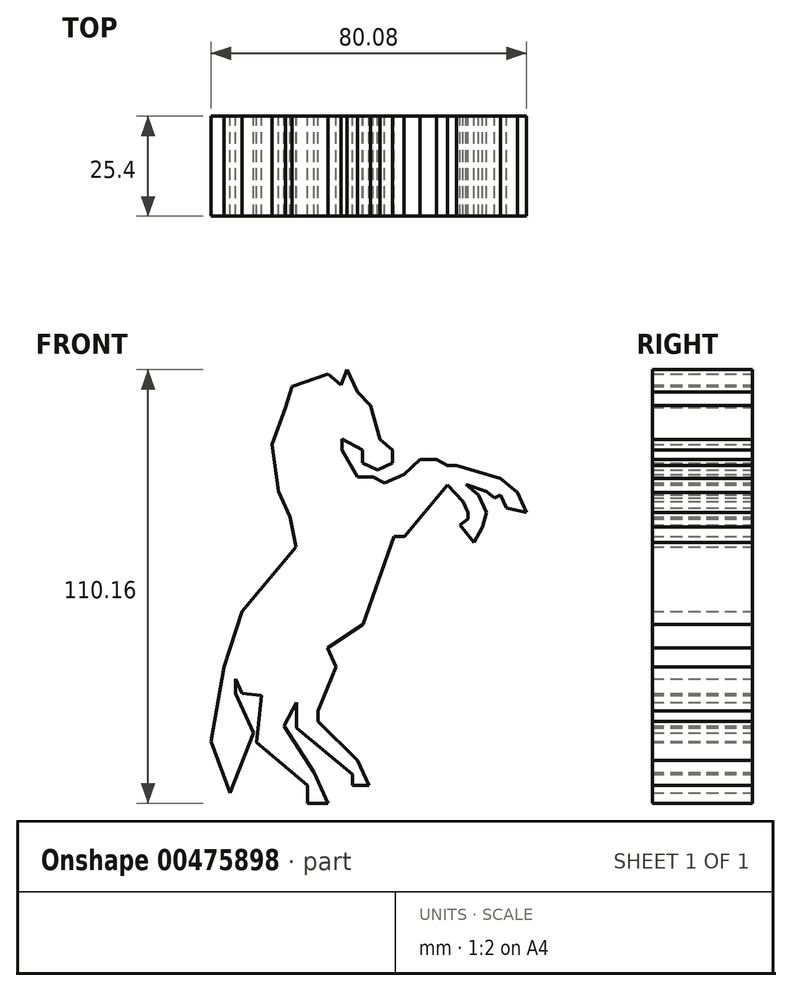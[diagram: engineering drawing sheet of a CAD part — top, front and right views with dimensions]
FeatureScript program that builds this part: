
annotation { "Feature Type Name" : "Feature", "Feature Type Description" : "" }
export const myFeature = defineFeature(function(context is Context, id is Id, definition is map)
    precondition{}
    {
        {
            var Q0;
            Q0=qCreatedBy(makeId("Front.planeOp"),FACE);
            var sketch = newSketch(context, id + "F0", { "sketchPlane" : qUnion([Q0])});
            skLineSegment(sketch, "E0", {"start": v(-2.68, 56.92) * mm, "end": v(0, 51.28) * mm});
            skLineSegment(sketch, "E1", {"start": v(0, 51.28) * mm, "end": v(3.22, 47.8) * mm});
            skLineSegment(sketch, "E2", {"start": v(3.22, 47.8) * mm, "end": v(5.64, 39.2) * mm});
            skLineSegment(sketch, "E3", {"start": v(5.64, 39.2) * mm, "end": v(8.86, 36.51) * mm});
            skLineSegment(sketch, "E4", {"start": v(8.86, 36.51) * mm, "end": v(8.86, 33.19) * mm});
            skLineSegment(sketch, "E5", {"start": v(8.86, 33.19) * mm, "end": v(5.1, 31.41) * mm});
            skLineSegment(sketch, "E6", {"start": v(5.1, 31.41) * mm, "end": v(1.26, 33.19) * mm});
            skLineSegment(sketch, "E7", {"start": v(1.26, 33.19) * mm, "end": v(1.26, 36.51) * mm});
            skLineSegment(sketch, "E8", {"start": v(1.26, 36.51) * mm, "end": v(-4, 39.32) * mm});
            skLineSegment(sketch, "E9", {"start": v(-4, 39.32) * mm, "end": v(-4, 36.51) * mm});
            skLineSegment(sketch, "E10", {"start": v(-4, 36.51) * mm, "end": v(0, 29.63) * mm});
            skLineSegment(sketch, "E11", {"start": v(0, 29.63) * mm, "end": v(3.95, 29.63) * mm});
            skLineSegment(sketch, "E12", {"start": v(3.95, 29.63) * mm, "end": v(6.8, 28.12) * mm});
            skLineSegment(sketch, "E13", {"start": v(6.8, 28.12) * mm, "end": v(11.8, 30.28) * mm});
            skLineSegment(sketch, "E14", {"start": v(11.8, 30.28) * mm, "end": v(15.79, 34.07) * mm});
            skLineSegment(sketch, "E15", {"start": v(15.79, 34.07) * mm, "end": v(20.03, 34.07) * mm});
            skLineSegment(sketch, "E16", {"start": v(20.03, 34.07) * mm, "end": v(22.83, 32.59) * mm});
            skLineSegment(sketch, "E17", {"start": v(22.83, 32.59) * mm, "end": v(25.15, 32.59) * mm});
            skLineSegment(sketch, "E18", {"start": v(25.15, 32.59) * mm, "end": v(36.34, 29.23) * mm});
            skLineSegment(sketch, "E19", {"start": v(36.34, 29.23) * mm, "end": v(40.54, 25.73) * mm});
            skLineSegment(sketch, "E20", {"start": v(40.54, 25.73) * mm, "end": v(42.86, 20.64) * mm});
            skLineSegment(sketch, "E21", {"start": v(42.86, 20.64) * mm, "end": v(37.86, 21.73) * mm});
            skLineSegment(sketch, "E22", {"start": v(37.86, 21.73) * mm, "end": v(36.34, 25.1) * mm});
            skLineSegment(sketch, "E23", {"start": v(36.34, 25.1) * mm, "end": v(34.74, 24.38) * mm});
            skLineSegment(sketch, "E24", {"start": v(34.74, 24.38) * mm, "end": v(32.76, 26.03) * mm});
            skLineSegment(sketch, "E25", {"start": v(32.76, 26.03) * mm, "end": v(27.5, 27.75) * mm});
            skLineSegment(sketch, "E26", {"start": v(27.5, 27.75) * mm, "end": v(30.68, 25.1) * mm});
            skLineSegment(sketch, "E27", {"start": v(30.68, 25.1) * mm, "end": v(32.7, 20.64) * mm});
            skLineSegment(sketch, "E28", {"start": v(32.7, 20.64) * mm, "end": v(31.7, 16.97) * mm});
            skLineSegment(sketch, "E29", {"start": v(31.7, 16.97) * mm, "end": v(29.58, 12.98) * mm});
            skLineSegment(sketch, "E30", {"start": v(29.58, 12.98) * mm, "end": v(26.03, 17.42) * mm});
            skLineSegment(sketch, "E31", {"start": v(26.03, 17.42) * mm, "end": v(28, 19) * mm});
            skLineSegment(sketch, "E32", {"start": v(28, 19) * mm, "end": v(28, 20.64) * mm});
            skLineSegment(sketch, "E33", {"start": v(28, 20.64) * mm, "end": v(26.76, 23.4) * mm});
            skLineSegment(sketch, "E34", {"start": v(26.76, 23.4) * mm, "end": v(22.83, 27.64) * mm});
            skLineSegment(sketch, "E35", {"start": v(22.83, 27.64) * mm, "end": v(11.92, 14.54) * mm});
            skLineSegment(sketch, "E36", {"start": v(11.92, 14.54) * mm, "end": v(9.23, 14.54) * mm});
            skLineSegment(sketch, "E37", {"start": v(9.23, 14.54) * mm, "end": v(1.4, -7.77) * mm});
            skLineSegment(sketch, "E38", {"start": v(1.4, -7.77) * mm, "end": v(-7.68, -13.79) * mm});
            skLineSegment(sketch, "E39", {"start": v(-7.68, -13.79) * mm, "end": v(-5.51, -18.58) * mm});
            skLineSegment(sketch, "E40", {"start": v(-5.51, -18.58) * mm, "end": v(-10.08, -29.81) * mm});
            skLineSegment(sketch, "E41", {"start": v(-10.08, -29.81) * mm, "end": v(-10.08, -32.43) * mm});
            skLineSegment(sketch, "E42", {"start": v(-10.08, -32.43) * mm, "end": v(0, -42.32) * mm});
            skLineSegment(sketch, "E43", {"start": v(0, -42.32) * mm, "end": v(2.87, -48.67) * mm});
            skLineSegment(sketch, "E44", {"start": v(2.87, -48.67) * mm, "end": v(-1.35, -48.67) * mm});
            skLineSegment(sketch, "E45", {"start": v(-1.35, -48.67) * mm, "end": v(-1.35, -45.96) * mm});
            skLineSegment(sketch, "E46", {"start": v(-1.35, -45.96) * mm, "end": v(-15.53, -34.14) * mm});
            skLineSegment(sketch, "E47", {"start": v(-15.53, -34.14) * mm, "end": v(-15.53, -27.63) * mm});
            skLineSegment(sketch, "E48", {"start": v(-15.53, -27.63) * mm, "end": v(-18.67, -33.54) * mm});
            skLineSegment(sketch, "E49", {"start": v(-18.67, -33.54) * mm, "end": v(-11.1, -45.37) * mm});
            skLineSegment(sketch, "E50", {"start": v(-11.1, -45.37) * mm, "end": v(-9.6, -48.67) * mm});
            skLineSegment(sketch, "E51", {"start": v(-9.6, -48.67) * mm, "end": v(-7.55, -53.24) * mm});
            skLineSegment(sketch, "E52", {"start": v(-7.55, -53.24) * mm, "end": v(-12.7, -53.24) * mm});
            skLineSegment(sketch, "E53", {"start": v(-12.7, -53.24) * mm, "end": v(-12.7, -48.67) * mm});
            skLineSegment(sketch, "E54", {"start": v(-12.7, -48.67) * mm, "end": v(-25.7, -37.83) * mm});
            skLineSegment(sketch, "E55", {"start": v(-25.7, -37.83) * mm, "end": v(-24.48, -25.89) * mm});
            skLineSegment(sketch, "E56", {"start": v(-24.48, -25.89) * mm, "end": v(-29.31, -25.4) * mm});
            skLineSegment(sketch, "E57", {"start": v(-29.31, -25.4) * mm, "end": v(-31.01, -21.63) * mm});
            skLineSegment(sketch, "E58", {"start": v(-31.01, -21.63) * mm, "end": v(-31.01, -25.4) * mm});
            skLineSegment(sketch, "E59", {"start": v(-31.01, -25.4) * mm, "end": v(-26.48, -35.42) * mm});
            skLineSegment(sketch, "E60", {"start": v(-26.48, -35.42) * mm, "end": v(-32.48, -50.56) * mm});
            skLineSegment(sketch, "E61", {"start": v(-32.48, -50.56) * mm, "end": v(-37.22, -37.49) * mm});
            skLineSegment(sketch, "E62", {"start": v(-37.22, -37.49) * mm, "end": v(-33.93, -18.58) * mm});
            skLineSegment(sketch, "E63", {"start": v(-33.93, -18.58) * mm, "end": v(-29.31, -4.51) * mm});
            skLineSegment(sketch, "E64", {"start": v(-29.31, -4.51) * mm, "end": v(-15.66, 11.87) * mm});
            skLineSegment(sketch, "E65", {"start": v(-15.66, 11.87) * mm, "end": v(-17.2, 19.54) * mm});
            skLineSegment(sketch, "E66", {"start": v(-17.2, 19.54) * mm, "end": v(-20.13, 26.03) * mm});
            skLineSegment(sketch, "E67", {"start": v(-20.13, 26.03) * mm, "end": v(-21.7, 37.95) * mm});
            skLineSegment(sketch, "E68", {"start": v(-21.7, 37.95) * mm, "end": v(-18.28, 47.27) * mm});
            skLineSegment(sketch, "E69", {"start": v(-18.28, 47.27) * mm, "end": v(-16.68, 52.66) * mm});
            skLineSegment(sketch, "E70", {"start": v(-16.68, 52.66) * mm, "end": v(-7.58, 55.86) * mm});
            skLineSegment(sketch, "E71", {"start": v(-7.58, 55.86) * mm, "end": v(-4.17, 53.02) * mm});
            skLineSegment(sketch, "E72", {"start": v(-4.17, 53.02) * mm, "end": v(-2.68, 56.92) * mm});
            skSolve(sketch);
        }
        {
            var Q0;
            Q0 = qSketchRegion(id + "F0", true);
            extrude(context, id + "F1", {"entities" : qUnion([Q0]), "depth" : 25.4 * mm});
        }
    });
